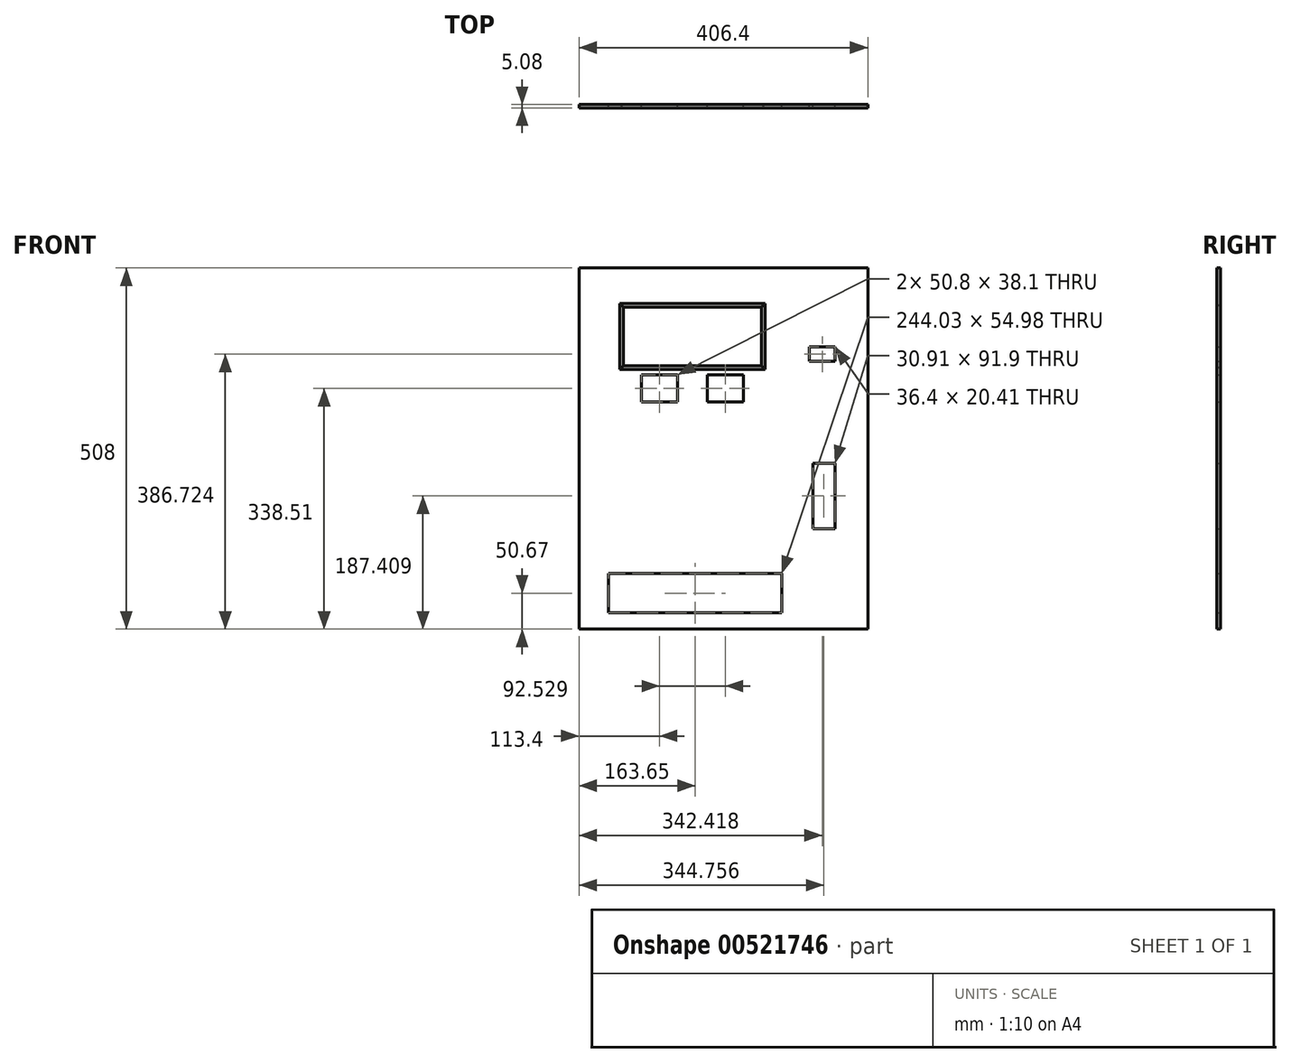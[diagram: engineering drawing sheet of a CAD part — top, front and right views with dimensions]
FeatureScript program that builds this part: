
annotation { "Feature Type Name" : "Feature", "Feature Type Description" : "" }
export const myFeature = defineFeature(function(context is Context, id is Id, definition is map)
    precondition{}
    {
        {
            var Q0;
            Q0=qCreatedBy(makeId("Front.planeOp"),FACE);
            var sketch = newSketch(context, id + "F0", { "sketchPlane" : qUnion([Q0])});
            skLineSegment(sketch, "E0.bottom", {"start": v(-202.3, 340.94) * mm, "end": v(204.1, 340.94) * mm});
            skLineSegment(sketch, "E0.top", {"start": v(-202.3, -167.06) * mm, "end": v(204.1, -167.06) * mm});
            skLineSegment(sketch, "E0.left", {"start": v(-202.3, 340.94) * mm, "end": v(-202.3, -167.06) * mm});
            skLineSegment(sketch, "E0.right", {"start": v(204.1, 340.94) * mm, "end": v(204.1, -167.06) * mm});
            skLineSegment(sketch, "E1.bottom", {"start": v(121.92, 209.46) * mm, "end": v(158.32, 209.46) * mm});
            skLineSegment(sketch, "E1.top", {"start": v(121.92, 229.87) * mm, "end": v(158.32, 229.87) * mm});
            skLineSegment(sketch, "E1.left", {"start": v(121.92, 229.87) * mm, "end": v(121.92, 209.46) * mm});
            skLineSegment(sketch, "E1.right", {"start": v(158.32, 229.87) * mm, "end": v(158.32, 209.46) * mm});
            skLineSegment(sketch, "E2.bottom", {"start": v(127, 66.3) * mm, "end": v(157.91, 66.3) * mm});
            skLineSegment(sketch, "E2.top", {"start": v(127, -25.6) * mm, "end": v(157.91, -25.6) * mm});
            skLineSegment(sketch, "E2.left", {"start": v(127, 66.3) * mm, "end": v(127, -25.6) * mm});
            skLineSegment(sketch, "E2.right", {"start": v(157.91, 66.3) * mm, "end": v(157.91, -25.6) * mm});
            skLineSegment(sketch, "E3.bottom", {"start": v(-114.3, 190.5) * mm, "end": v(-63.5, 190.5) * mm});
            skLineSegment(sketch, "E3.top", {"start": v(-114.3, 152.4) * mm, "end": v(-63.5, 152.4) * mm});
            skLineSegment(sketch, "E3.left", {"start": v(-114.3, 190.5) * mm, "end": v(-114.3, 152.4) * mm});
            skLineSegment(sketch, "E3.right", {"start": v(-63.5, 190.5) * mm, "end": v(-63.5, 152.4) * mm});
            skLineSegment(sketch, "E4.bottom", {"start": v(-21.77, 190.5) * mm, "end": v(29.03, 190.5) * mm});
            skLineSegment(sketch, "E4.top", {"start": v(-21.77, 152.4) * mm, "end": v(29.03, 152.4) * mm});
            skLineSegment(sketch, "E4.left", {"start": v(-21.77, 190.5) * mm, "end": v(-21.77, 152.4) * mm});
            skLineSegment(sketch, "E4.right", {"start": v(29.03, 190.5) * mm, "end": v(29.03, 152.4) * mm});
            skLineSegment(sketch, "E5.bottom", {"start": v(-139.7, 285.68) * mm, "end": v(54.43, 285.68) * mm});
            skLineSegment(sketch, "E5.top", {"start": v(-139.7, 203.2) * mm, "end": v(54.43, 203.2) * mm});
            skLineSegment(sketch, "E5.left", {"start": v(-139.7, 285.68) * mm, "end": v(-139.7, 203.2) * mm});
            skLineSegment(sketch, "E5.right", {"start": v(54.43, 285.68) * mm, "end": v(54.43, 203.2) * mm});
            skPoint(sketch, "E6.bottom.start.orphan", {"position": v(-149.1, 0) * mm});
            skPoint(sketch, "E6.right.start.orphan", {"position": v(62.8, 0) * mm});
            skLineSegment(sketch, "E7.bottom", {"start": v(-160.67, -88.9) * mm, "end": v(83.37, -88.9) * mm});
            skLineSegment(sketch, "E7.top", {"start": v(-160.67, -143.88) * mm, "end": v(83.37, -143.88) * mm});
            skLineSegment(sketch, "E7.left", {"start": v(-160.67, -88.9) * mm, "end": v(-160.67, -143.88) * mm});
            skLineSegment(sketch, "E7.right", {"start": v(83.37, -88.9) * mm, "end": v(83.37, -143.88) * mm});
            skSolve(sketch);
        }
        {
            var Q0;
            Q0 = qSketchRegion(id + "F0", true);
            extrude(context, id + "F1", {"entities" : qUnion([Q0]), "depth" : 5.08 * mm, "offsetDistance" : 25.4 * mm});
        }
        {
            var Q0;
            Q0=makeQuery(id+"F1.opExtrude","CAP_EDGE",EDGE,{"disambiguationData":[OSD([sQuery(id+"F0.wireOp",EDGE,"E5.left")])],"isStart":false});
            var Q1;
            Q1=makeQuery(id+"F1.opExtrude","CAP_EDGE",EDGE,{"disambiguationData":[OSD([sQuery(id+"F0.wireOp",EDGE,"E5.bottom")])],"isStart":false});
            var Q2;
            Q2=makeQuery(id+"F1.opExtrude","CAP_EDGE",EDGE,{"disambiguationData":[OSD([sQuery(id+"F0.wireOp",EDGE,"E5.right")])],"isStart":false});
            var Q3;
            Q3=makeQuery(id+"F1.opExtrude","CAP_EDGE",EDGE,{"disambiguationData":[OSD([sQuery(id+"F0.wireOp",EDGE,"E5.top")])],"isStart":false});
            chamfer(context, id + "F2", {"entities" : qUnion([Q0, Q1, Q2, Q3]), "width" : 5.08 * mm, "tangentPropagation" : true});
        }
    });
